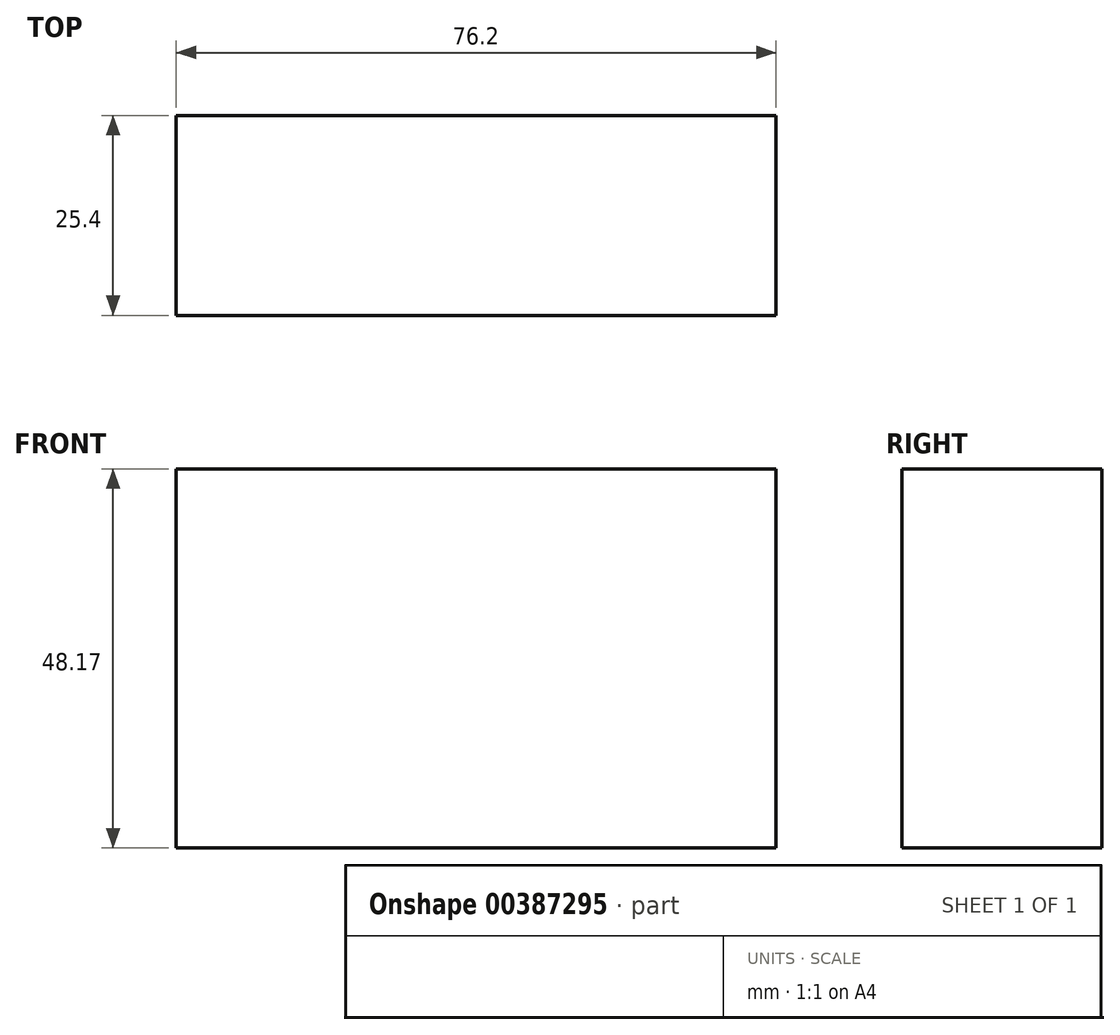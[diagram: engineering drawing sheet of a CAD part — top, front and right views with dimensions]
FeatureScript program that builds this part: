
annotation { "Feature Type Name" : "Feature", "Feature Type Description" : "" }
export const myFeature = defineFeature(function(context is Context, id is Id, definition is map)
    precondition{}
    {
        {
            var Q0;
            Q0=qCreatedBy(makeId("Front.planeOp"),FACE);
            var sketch = newSketch(context, id + "F0", { "sketchPlane" : qUnion([Q0])});
            skLineSegment(sketch, "E0.bottom", {"start": v(0, 0) * mm, "end": v(25.4, 0) * mm});
            skLineSegment(sketch, "E0.top", {"start": v(0, 25.4) * mm, "end": v(25.4, 25.4) * mm});
            skLineSegment(sketch, "E0.left", {"start": v(0, 0) * mm, "end": v(0, 25.4) * mm});
            skLineSegment(sketch, "E0.right", {"start": v(25.4, 0) * mm, "end": v(25.4, 25.4) * mm});
            skLineSegment(sketch, "E1.bottom", {"start": v(0, 0) * mm, "end": v(-25.4, 0) * mm});
            skLineSegment(sketch, "E1.top", {"start": v(0, 25.4) * mm, "end": v(-25.4, 25.4) * mm});
            skLineSegment(sketch, "E1.right", {"start": v(-25.4, 0) * mm, "end": v(-25.4, 25.4) * mm});
            skLineSegment(sketch, "E2.bottom", {"start": v(25.4, 25.4) * mm, "end": v(50.8, 25.4) * mm});
            skLineSegment(sketch, "E2.top", {"start": v(25.4, 0) * mm, "end": v(50.8, 0) * mm});
            skLineSegment(sketch, "E2.left", {"start": v(25.4, 25.4) * mm, "end": v(25.4, 0) * mm});
            skLineSegment(sketch, "E2.right", {"start": v(50.8, 25.4) * mm, "end": v(50.8, 0) * mm});
            skLineSegment(sketch, "E3.bottom", {"start": v(-25.4, 25.4) * mm, "end": v(0, 25.4) * mm});
            skLineSegment(sketch, "E3.top", {"start": v(-25.4, 48.17) * mm, "end": v(0, 48.17) * mm});
            skLineSegment(sketch, "E3.left", {"start": v(-25.4, 25.4) * mm, "end": v(-25.4, 48.17) * mm});
            skLineSegment(sketch, "E3.right", {"start": v(0, 25.4) * mm, "end": v(0, 48.17) * mm});
            skLineSegment(sketch, "E4.bottom", {"start": v(0, 48.17) * mm, "end": v(25.4, 48.17) * mm});
            skLineSegment(sketch, "E4.left", {"start": v(0, 48.17) * mm, "end": v(0, 25.4) * mm});
            skLineSegment(sketch, "E4.right", {"start": v(25.4, 48.17) * mm, "end": v(25.4, 25.4) * mm});
            skLineSegment(sketch, "E5.bottom", {"start": v(25.4, 48.17) * mm, "end": v(50.8, 48.17) * mm});
            skLineSegment(sketch, "E5.right", {"start": v(50.8, 48.17) * mm, "end": v(50.8, 25.4) * mm});
            skSolve(sketch);
        }
        {
            var Q0;
            Q0=makeQuery(id+"F0.imprint","IMPRINT",FACE,{"disambiguationData":[TD([[makeQuery(id+"F0.imprint","IMPRINT",EDGE,{"derivedFrom":sQuery(id+"F0.wireOp",EDGE,"E2.top")}),1.0]])]});
            var Q1;
            Q1=makeQuery(id+"F0.imprint","IMPRINT",FACE,{"disambiguationData":[TD([[makeQuery(id+"F0.imprint","IMPRINT",EDGE,{"derivedFrom":sQuery(id+"F0.wireOp",EDGE,"E3.bottom")}),1.0]])]});
            var Q2;
            Q2=makeQuery(id+"F0.imprint","IMPRINT",FACE,{"disambiguationData":[TD([[makeQuery(id+"F0.imprint","IMPRINT",EDGE,{"derivedFrom":sQuery(id+"F0.wireOp",EDGE,"E5.bottom")}),-1.0]])]});
            var Q3;
            Q3=makeQuery(id+"F0.imprint","IMPRINT",FACE,{"disambiguationData":[TD([[makeQuery(id+"F0.imprint","IMPRINT",EDGE,{"derivedFrom":sQuery(id+"F0.wireOp",EDGE,"E0.bottom")}),1.0]])]});
            var Q4;
            Q4=makeQuery(id+"F0.imprint","IMPRINT",FACE,{"disambiguationData":[TD([[makeQuery(id+"F0.imprint","IMPRINT",EDGE,{"derivedFrom":sQuery(id+"F0.wireOp",EDGE,"E4.bottom")}),-1.0]])]});
            var Q5;
            Q5=makeQuery(id+"F0.imprint","IMPRINT",FACE,{"disambiguationData":[TD([[makeQuery(id+"F0.imprint","IMPRINT",EDGE,{"derivedFrom":sQuery(id+"F0.wireOp",EDGE,"E1.bottom")}),-1.0]])]});
            extrude(context, id + "F1", {"entities" : qUnion([Q0, Q1, Q2, Q3, Q4, Q5]), "depth" : 25.4 * mm});
        }
        {
            var Q0;
            Q0 = qSketchRegion(id + "F0", true);
            extrude(context, id + "F2", {"entities" : qUnion([Q0]), "operationType" : NewBodyOperationType.ADD, "depth" : 25.4 * mm});
        }
    });
